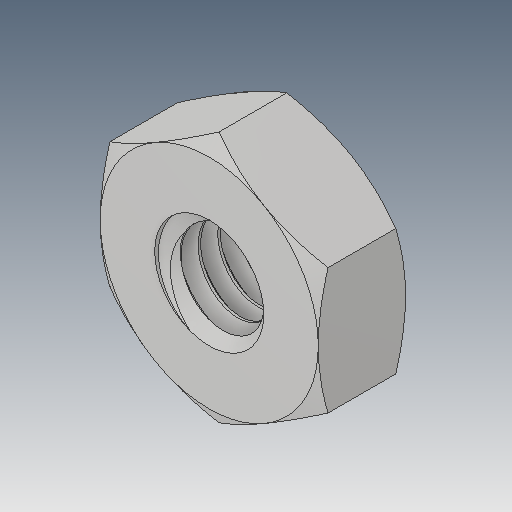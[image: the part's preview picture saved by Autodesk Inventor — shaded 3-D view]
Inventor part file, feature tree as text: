
AUTODESK INVENTOR PART (.ipt)
format: ipt  version: 2017 (Build 210142000, 142)  size: 281,088 bytes
history: mixed  units: in
note: dims shown in document units (in); Inventor stores cm internally (conversion verified against a paired STEP export)
features: mirror x1, imported_body x1
ambient origin geometry x8: Origin, YZ Plane, XZ Plane, XY Plane, X Axis, Y Axis, Z Axis, Center Point
bodies: Solid1 (imported_parasolid)
feature tree (2):
  mirror  "Mirror2"
  imported_body  NMx_Import_Brep_tag  [imported B-rep: ~6 faces, bbox_mm=None]
